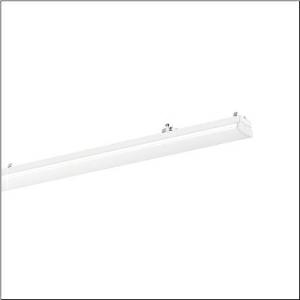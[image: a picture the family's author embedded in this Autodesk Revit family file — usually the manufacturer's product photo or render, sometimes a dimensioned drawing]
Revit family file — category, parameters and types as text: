
# Revit family: licross_11_recessed_opal_mo_51tl1ddv495g
name_source: partatom
category: Lighting Fixtures
units: mm (PartAtom-declared; Revit-internal decimal feet)

## family parameters
Cut with Voids When Loaded = No
Host = Face
Light Source = No
Part Type = Normal
Room Calculation Point = No
Round Connector Dimension = Use Diameter
Shared = No

## types (1)
- --- (1 x LED, 9500 lm, 52.6 W, 4000K)
    Apparent Load = 53 VA
    CIE Flux Codes = 44 73 91 87 100
    Color Rendering = 80
    Color Temperature = 4000K
    Default Elevation = 1800 mm
    Description = Licross 11 recessed opal MO, luminaire insert, of sheet steel, coil coated, white, length: 2.250mm, width: 76mm, height: 87mm, LED rated luminous flux: 9.500lm, light colour: 840, SDCM (Standard Deviation of Colour Matching)MacAdam ≤ 2 SDCM (initial), control gear: DALI 2, with plug, 5-pole, with phase selection, mains connection: 220..240V, AC, 50/60Hz, rated input power: 53W, internal wiring halogen-free, primary optical cover: cover, of PMMA, light emission: direct with ceiling illumination distribution, primary light characteristic: symmetric, protection rating (complete): IP40, insulation class (complete): insulation class I (protective earthing), certification: CE, ENEC, VDE, UKCA, protection symbol: D if used in an environment without relevant dust loads with corresponding accessories, impact resistance: IK06, permissible ambient temperature for indoor applications: -25..+40°C, corresponds to IFS (International Featured Standards) requirements for safety and quality in the food industry, reducing of maximum allowable ambient temperature of 5°C with ceiling mounting, LABS conformity tested according to VDMA 24364:2018-05, The light source and the operating device comply with the requirements of the Ecodesign Regulation (EU) 2019/2020 and are replaceable in accordance with this regulation, packaging unit: 1 piece
    Height = 83 mm
    Lamp = 1 x LED
    Lamp Light Flux = 9500 lm
    Lamp Power = 52.6 W
    Lamp count = 1
    Length = 2250 mm
    Luminous efficacy = 181 lm/W
    Manufacturer = Siteco
    ModVariant = No
    Model = 51TL1DDV495G
    Mounting Place = Ceiling
    Mounting Type = Pendant
    Number of Poles = 1
    OnlyDefault = Yes
    Power Factor = 1
    Product Name = Licross 11 recessed opal MO
    Product group = luminaire insert | ceiling pendant
    ProductGroupID = 901
    Protection Class = Protection class I
    Protection Degree = IP 40
    RLX_Detail_Level = 1
    RLX_Emergency_Light_Flux = 0 lm
    RLX_Emergency_Type = 0
    RLX_Emergency_Type_DB = No
    RlxData = <blob elided: 26877 chars, md5=cbf105f9>
    Socket = socket
    Standby Power = 0 W
    System Light Flux = 9500 lm
    System Power = 53 W
    Type Comments = factory setting: luminous flux: 100 % | dim-lin: 254 | 239 mA
    Type Image = l_1313666.jpg
    URL = http://relux.com
    VarID = @adj_084253
    Voltage = 0 V
    Weight = 0.00 kg
    Width = 76 mm

## geometry (parser evidence)
native form markers: Blend x4, Sweep x14
no freeform markers — native parametric forms only
